# Revit family: THB75
name_source: partatom
category: Generic Models
revit_build: Autodesk Revit LT 2017 (Build: 20160225_1515(x64)
units: mm (PartAtom-declared; Revit-internal decimal feet)

## family parameters
Always vertical = No
Can host rebar = No
Cut with Voids When Loaded = No
Part Type = Normal
Room Calculation Point = No
Round Connector Dimension = Use Diameter
Shared = No
Work Plane-Based = Yes

## types (1)
- NBS Standard Parameters
    BIMObjectName = Metpro_metprolibrary_cabletrunking_supportsystem_tophatbracket
    Default Elevation = 1219 mm
    Description = THB75  - 75mm Top Hat Bracket
    DurationUnit = year
    Finish = Pre Galvanised
    Keynote = Compliant to LU Standard 1-085
    ManufacturerName = Metpro Ltd
    ManufacturerURL = www.metpro.co.uk
    Material = Pre Galvanised Material
    ModelReference = THB75
    NBSDescription = Cable Trunking
    NBSReference = 90-55-10/410
    NominalHeight = 26 mm
    NominalLength = 122 mm  [stored 0.400262 ft]
    NominalWidth = 29 mm
    ProductInformation = www.metpro.co.uk/pdf/thb75.pdf
    Size = 75
    Uniclass2 = PR_65_701_11_18
    Version = 1
    WarrantyDurationUnit = 1 year
    Weight = 0.059Kg

note: [stored X ft] marks values corroborated as IEEE doubles in the binary element streams (Revit-internal decimal feet)

## geometry (parser evidence)
native form markers: Sweep x2
no freeform markers — native parametric forms only
